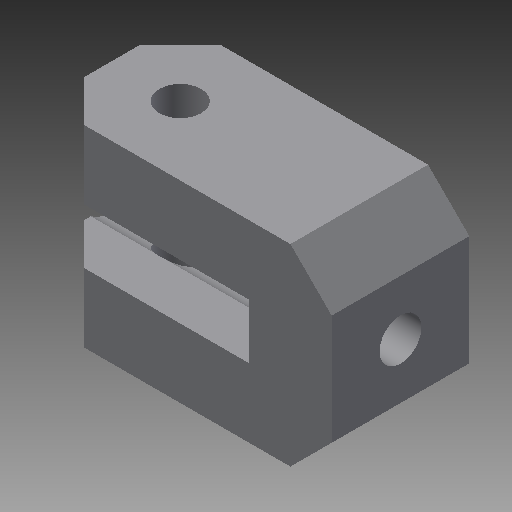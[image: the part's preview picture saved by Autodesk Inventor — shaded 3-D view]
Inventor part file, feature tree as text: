
AUTODESK INVENTOR PART (.ipt)
format: ipt  version: 2017 SP1 (Build 210196100, 196)  size: 145,408 bytes
history: native  units: mm
features: extrude x4, sketch x4, chamfer x2
ambient origin geometry x8: Origin, YZ Plane, XZ Plane, XY Plane, X Axis, Y Axis, Z Axis, Center Point
bodies: Solid1 (feature_tree)
feature tree (10):
  extrude  "Extrusion1"  Depth=10.0mm
  extrude  "Extrusion2"  Depth=12.0mm
  extrude  "Extrusion3"  Depth=20.0mm TaperAngle=0.0deg
  extrude  "Extrusion4"  Depth=20.0mm TaperAngle=0.0deg
  chamfer  "Chamfer1"  Distance=17.0mm
  chamfer  "Chamfer2"  Distance=6.1mm
  sketch  "Sketch1"  dims[d0=8.0mm d1=10.0mm]
  sketch  "Sketch2"  dims[d2=10.0mm d3=12.0mm]
  sketch  "Sketch3"  dims[d4=30.0mm d5=20.0mm d6=0.0mm]
  sketch  "Sketch4"  dims[d7=6.1mm d8=20.0mm d9=0.0mm d10=17.0mm d11=6.1mm d12=20.0mm d13=20.0mm d14=0.0mm d15=10.0mm d16=20.0mm d17=0.0mm d18=6.0mm d19=2.0mm d20=45.0deg d21=6.0mm d22=2.0mm d23=45.0deg d24=11.5mm d25=32.0mm]
